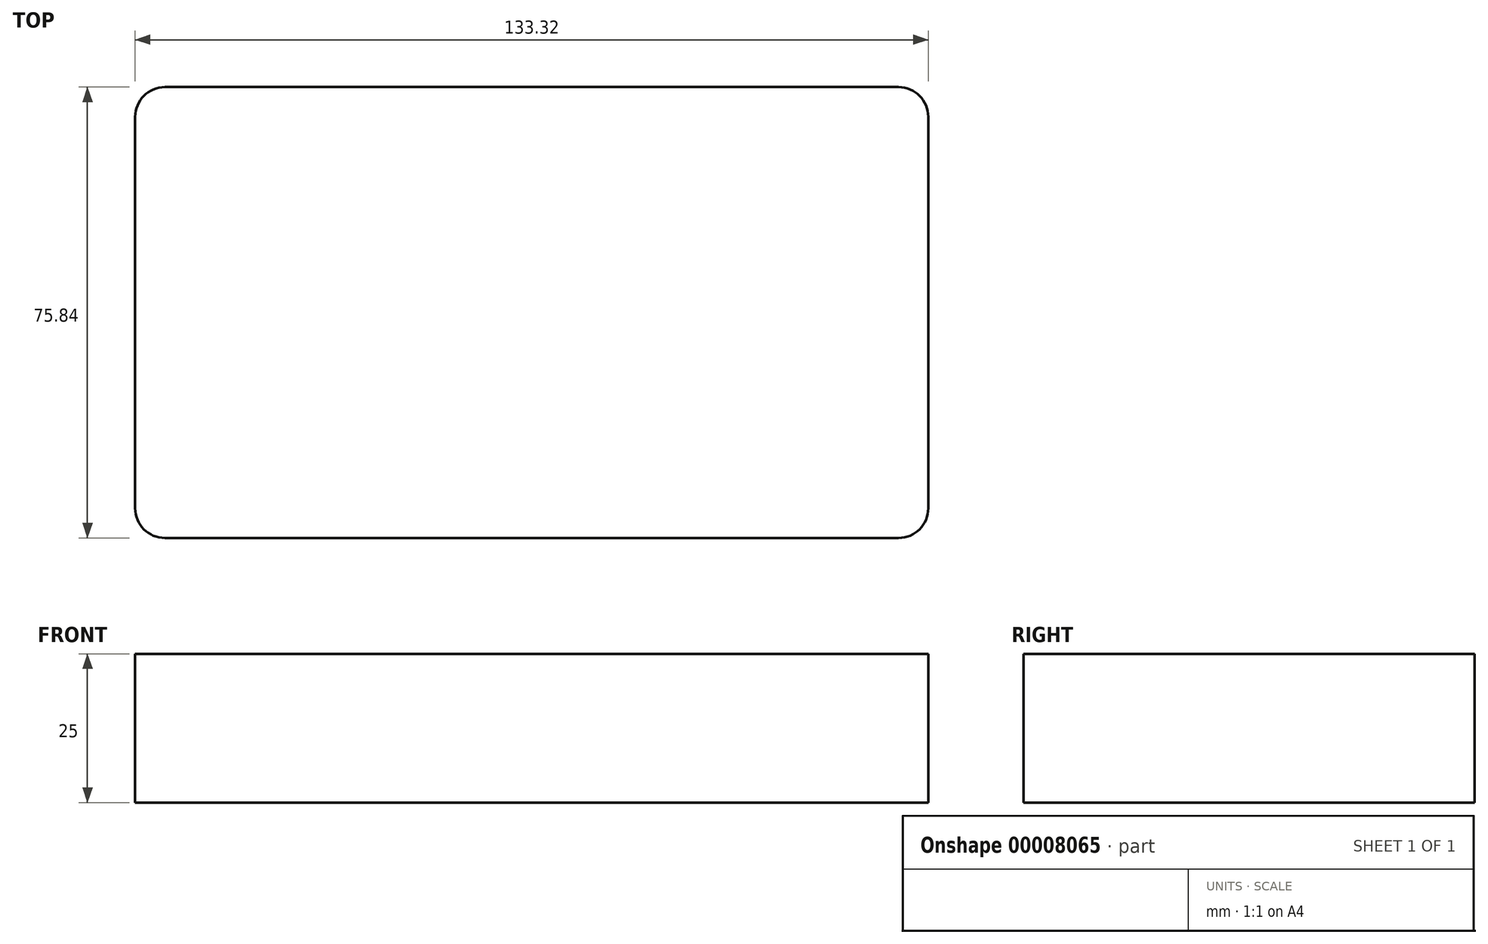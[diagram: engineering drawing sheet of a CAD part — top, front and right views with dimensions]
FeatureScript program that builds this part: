
annotation { "Feature Type Name" : "Feature", "Feature Type Description" : "" }
export const myFeature = defineFeature(function(context is Context, id is Id, definition is map)
    precondition{}
    {
        {
            var Q0;
            Q0=qCreatedBy(makeId("Top.planeOp"),FACE);
            var sketch = newSketch(context, id + "F0", { "sketchPlane" : qUnion([Q0])});
            skLineSegment(sketch, "E0.bottom", {"start": v(-49.9, 39.08) * mm, "end": v(73.41, 39.08) * mm});
            skLineSegment(sketch, "E0.top", {"start": v(-49.9, -36.76) * mm, "end": v(73.41, -36.76) * mm});
            skLineSegment(sketch, "E0.left", {"start": v(-54.9, 34.08) * mm, "end": v(-54.9, -31.76) * mm});
            skLineSegment(sketch, "E0.right", {"start": v(78.41, 34.08) * mm, "end": v(78.41, -31.76) * mm});
            skPoint(sketch, "E1.visualSharp", {"position": v(-54.9, -36.76) * mm});
            skArc(sketch, "E1.filletArc", {"start": v(-54.9, -31.76) * mm, "mid": v(-53.44, -35.3) * mm, "end": v(-49.9, -36.76) * mm});
            skPoint(sketch, "E2.visualSharp", {"position": v(78.41, -36.76) * mm});
            skArc(sketch, "E2.filletArc", {"start": v(73.41, -36.76) * mm, "mid": v(76.95, -35.3) * mm, "end": v(78.41, -31.76) * mm});
            skPoint(sketch, "E3.visualSharp", {"position": v(78.41, 39.08) * mm});
            skArc(sketch, "E3.filletArc", {"start": v(78.41, 34.08) * mm, "mid": v(76.95, 37.62) * mm, "end": v(73.41, 39.08) * mm});
            skPoint(sketch, "E4.visualSharp", {"position": v(-54.9, 39.08) * mm});
            skArc(sketch, "E4.filletArc", {"start": v(-49.9, 39.08) * mm, "mid": v(-53.44, 37.62) * mm, "end": v(-54.9, 34.08) * mm});
            skSolve(sketch);
        }
        {
            var Q0;
            Q0 = qSketchRegion(id + "F0", true);
            extrude(context, id + "F1", {"entities" : qUnion([Q0]), "depth" : 25 * mm});
        }
    });
